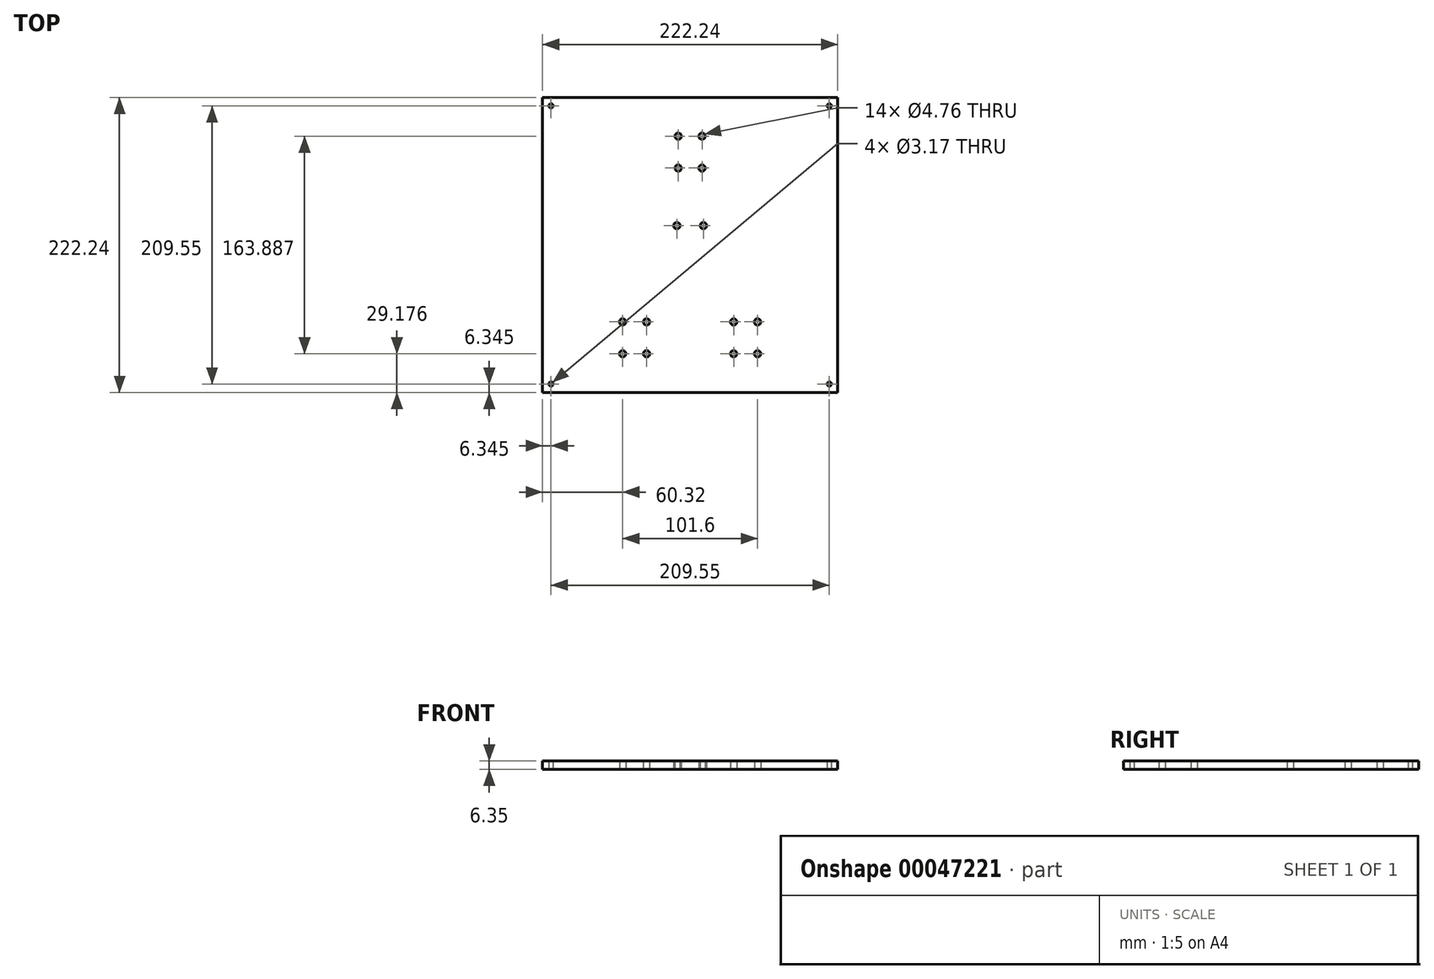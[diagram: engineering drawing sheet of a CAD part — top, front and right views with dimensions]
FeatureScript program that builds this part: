
annotation { "Feature Type Name" : "Feature", "Feature Type Description" : "" }
export const myFeature = defineFeature(function(context is Context, id is Id, definition is map)
    precondition{}
    {
        {
            var Q0;
            Q0=qCreatedBy(makeId("Top.planeOp"),FACE);
            var sketch = newSketch(context, id + "F0", { "sketchPlane" : qUnion([Q0])});
            skLineSegment(sketch, "E0.rect.bottom", {"start": v(111.13, 111.13) * mm, "end": v(-111.12, 111.13) * mm});
            skLineSegment(sketch, "E0.rect.top", {"start": v(111.13, -111.12) * mm, "end": v(-111.13, -111.12) * mm});
            skLineSegment(sketch, "E0.rect.left", {"start": v(111.13, 111.13) * mm, "end": v(111.13, -111.12) * mm});
            skLineSegment(sketch, "E0.rect.right", {"start": v(-111.13, 111.12) * mm, "end": v(-111.13, -111.12) * mm});
            skPoint(sketch, "E0.rect.middle", {"position": v(0, 0) * mm});
            skLineSegment(sketch, "E1.rect.bottom", {"start": v(104.78, 104.78) * mm, "end": v(-104.78, 104.78) * mm, "construction": true});
            skLineSegment(sketch, "E1.rect.top", {"start": v(104.78, -104.78) * mm, "end": v(-104.78, -104.78) * mm, "construction": true});
            skLineSegment(sketch, "E1.rect.left", {"start": v(104.78, 104.78) * mm, "end": v(104.78, -104.78) * mm, "construction": true});
            skLineSegment(sketch, "E1.rect.right", {"start": v(-104.77, 104.78) * mm, "end": v(-104.78, -104.78) * mm, "construction": true});
            skCircle(sketch, "E2", {"center": v(-104.78, 104.78) * mm, "radius": 1.59 * mm});
            skCircle(sketch, "E3", {"center": v(104.78, 104.78) * mm, "radius": 1.59 * mm});
            skCircle(sketch, "E4", {"center": v(104.78, -104.78) * mm, "radius": 1.59 * mm});
            skCircle(sketch, "E5", {"center": v(-104.78, -104.78) * mm, "radius": 1.59 * mm});
            skLineSegment(sketch, "E6", {"start": v(-50.8, 111.13) * mm, "end": v(-50.8, -111.12) * mm, "construction": true});
            skLineSegment(sketch, "E7", {"start": v(0, 111.12) * mm, "end": v(0, -111.12) * mm, "construction": true});
            skCircle(sketch, "E8", {"center": v(-50.8, -57.94) * mm, "radius": 2.38 * mm});
            skCircle(sketch, "E9", {"center": v(-32.8, -57.94) * mm, "radius": 2.38 * mm});
            skCircle(sketch, "E10", {"center": v(-50.8, -81.94) * mm, "radius": 2.38 * mm});
            skCircle(sketch, "E11", {"center": v(-32.8, -81.94) * mm, "radius": 2.38 * mm});
            skCircle(sketch, "E12", {"center": v(-9, 57.94) * mm, "radius": 2.38 * mm});
            skCircle(sketch, "E13", {"center": v(-9, 81.94) * mm, "radius": 2.38 * mm});
            skCircle(sketch, "E14", {"center": v(-10, 14.56) * mm, "radius": 2.38 * mm});
            skLineSegment(sketch, "E15", {"start": v(-9, 81.94) * mm, "end": v(-9, 111.13) * mm, "construction": true});
            skLineSegment(sketch, "E16", {"start": v(-32.8, -81.94) * mm, "end": v(-32.8, -111.12) * mm, "construction": true});
            skCircle(sketch, "E17.MirrorC", {"center": v(32.8, -81.94) * mm, "radius": 2.38 * mm});
            skCircle(sketch, "E18.MirrorC", {"center": v(50.8, -81.94) * mm, "radius": 2.38 * mm});
            skCircle(sketch, "E19.MirrorC", {"center": v(50.8, -57.94) * mm, "radius": 2.38 * mm});
            skCircle(sketch, "E20.MirrorC", {"center": v(32.8, -57.94) * mm, "radius": 2.38 * mm});
            skCircle(sketch, "E21.MirrorC", {"center": v(10, 14.56) * mm, "radius": 2.38 * mm});
            skCircle(sketch, "E22.MirrorC", {"center": v(9, 57.94) * mm, "radius": 2.38 * mm});
            skCircle(sketch, "E23.MirrorC", {"center": v(9, 81.94) * mm, "radius": 2.38 * mm});
            skSolve(sketch);
        }
        {
            var Q0;
            Q0 = qSketchRegion(id + "F0", true);
            extrude(context, id + "F1", {"entities" : qUnion([Q0]), "depth" : 6.35 * mm});
        }
    });
